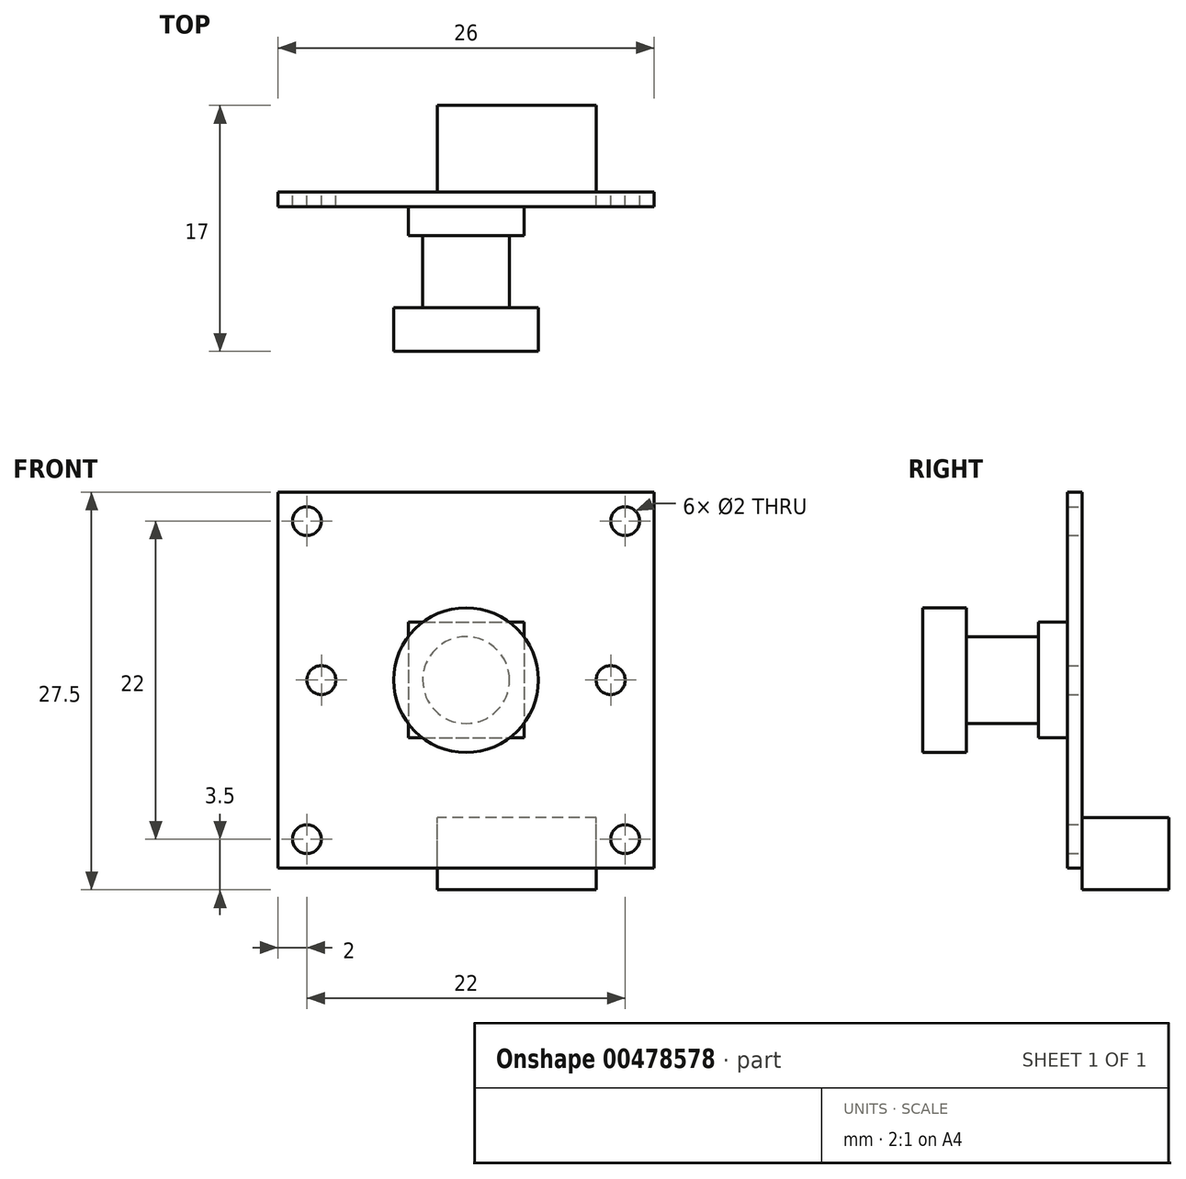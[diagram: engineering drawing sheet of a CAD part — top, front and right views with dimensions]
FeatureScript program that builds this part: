
annotation { "Feature Type Name" : "Feature", "Feature Type Description" : "" }
export const myFeature = defineFeature(function(context is Context, id is Id, definition is map)
    precondition{}
    {
        {
            var Q0;
            Q0=qCreatedBy(makeId("Front.planeOp"),FACE);
            var sketch = newSketch(context, id + "F0", { "sketchPlane" : qUnion([Q0])});
            skLineSegment(sketch, "E0.bottom", {"start": v(-13, 13) * mm, "end": v(13, 13) * mm});
            skLineSegment(sketch, "E0.top", {"start": v(-13, -13) * mm, "end": v(13, -13) * mm});
            skLineSegment(sketch, "E0.left", {"start": v(-13, 13) * mm, "end": v(-13, -13) * mm});
            skLineSegment(sketch, "E0.right", {"start": v(13, 13) * mm, "end": v(13, -13) * mm});
            skPoint(sketch, "E0.middle", {"position": v(0, 0) * mm});
            skLineSegment(sketch, "E1.bottom", {"start": v(-11, 11) * mm, "end": v(11, 11) * mm, "construction": true});
            skLineSegment(sketch, "E1.top", {"start": v(-11, -11) * mm, "end": v(11, -11) * mm, "construction": true});
            skLineSegment(sketch, "E1.left", {"start": v(-11, 11) * mm, "end": v(-11, -11) * mm, "construction": true});
            skLineSegment(sketch, "E1.right", {"start": v(11, 11) * mm, "end": v(11, -11) * mm, "construction": true});
            skCircle(sketch, "E2", {"center": v(-11, 11) * mm, "radius": 1 * mm});
            skCircle(sketch, "E3", {"center": v(11, 11) * mm, "radius": 1 * mm});
            skCircle(sketch, "E4", {"center": v(11, -11) * mm, "radius": 1 * mm});
            skCircle(sketch, "E5", {"center": v(-11, -11) * mm, "radius": 1 * mm});
            skLineSegment(sketch, "E6", {"start": v(0, 0) * mm, "end": v(-10, 0) * mm, "construction": true});
            skCircle(sketch, "E7", {"center": v(-10, 0) * mm, "radius": 1 * mm});
            skLineSegment(sketch, "E8", {"start": v(0, 0) * mm, "end": v(10, 0) * mm, "construction": true});
            skCircle(sketch, "E9", {"center": v(10, 0) * mm, "radius": 1 * mm});
            skSolve(sketch);
        }
        {
            var Q0;
            Q0 = qSketchRegion(id + "F0", true);
            extrude(context, id + "F1", {"entities" : qUnion([Q0]), "depth" : 1 * mm, "offsetDistance" : 25 * mm});
        }
        {
            var Q0;
            Q0=makeQuery(id+"F1.opExtrude","CAP_FACE",FACE,{"disambiguationData":[OSD([sQuery(id+"F0.wireOp",EDGE,"E0.bottom"),sQuery(id+"F0.wireOp",EDGE,"E0.top"),sQuery(id+"F0.wireOp",EDGE,"E0.left"),sQuery(id+"F0.wireOp",EDGE,"E0.right"),sQuery(id+"F0.wireOp",EDGE,"E2"),sQuery(id+"F0.wireOp",EDGE,"E3"),sQuery(id+"F0.wireOp",EDGE,"E4"),sQuery(id+"F0.wireOp",EDGE,"E5")])],"isStart":true});
            var sketch = newSketch(context, id + "F2", { "sketchPlane" : qUnion([Q0])});
            skLineSegment(sketch, "E10.bottom", {"start": v(-9, -14.5) * mm, "end": v(2, -14.5) * mm});
            skLineSegment(sketch, "E10.top", {"start": v(-9, -9.5) * mm, "end": v(2, -9.5) * mm});
            skLineSegment(sketch, "E10.left", {"start": v(-9, -14.5) * mm, "end": v(-9, -9.5) * mm});
            skLineSegment(sketch, "E10.right", {"start": v(2, -14.5) * mm, "end": v(2, -9.5) * mm});
            skPoint(sketch, "E10.middle", {"position": v(-3.5, -12) * mm});
            skSolve(sketch);
        }
        {
            var Q0;
            Q0 = qSketchRegion(id + "F2", true);
            extrude(context, id + "F3", {"entities" : qUnion([Q0]), "operationType" : NewBodyOperationType.ADD, "depth" : 6 * mm, "offsetDistance" : 25 * mm});
        }
        {
            var Q0;
            Q0=makeQuery(id+"F1.opExtrude","CAP_FACE",FACE,{"disambiguationData":[OSD([sQuery(id+"F0.wireOp",EDGE,"E0.bottom"),sQuery(id+"F0.wireOp",EDGE,"E0.top"),sQuery(id+"F0.wireOp",EDGE,"E0.left"),sQuery(id+"F0.wireOp",EDGE,"E0.right"),sQuery(id+"F0.wireOp",EDGE,"E2"),sQuery(id+"F0.wireOp",EDGE,"E3"),sQuery(id+"F0.wireOp",EDGE,"E4"),sQuery(id+"F0.wireOp",EDGE,"E5"),sQuery(id+"F0.wireOp",EDGE,"E7"),sQuery(id+"F0.wireOp",EDGE,"E9")])],"isStart":false});
            var sketch = newSketch(context, id + "F4", { "sketchPlane" : qUnion([Q0])});
            skLineSegment(sketch, "E11.bottom", {"start": v(-4, 4) * mm, "end": v(4, 4) * mm});
            skLineSegment(sketch, "E11.top", {"start": v(-4, -4) * mm, "end": v(4, -4) * mm});
            skLineSegment(sketch, "E11.left", {"start": v(-4, 4) * mm, "end": v(-4, -4) * mm});
            skLineSegment(sketch, "E11.right", {"start": v(4, 4) * mm, "end": v(4, -4) * mm});
            skPoint(sketch, "E11.middle", {"position": v(0, 0) * mm});
            skSolve(sketch);
        }
        {
            var Q0;
            Q0 = qSketchRegion(id + "F4", true);
            extrude(context, id + "F5", {"entities" : qUnion([Q0]), "operationType" : NewBodyOperationType.ADD, "depth" : 2 * mm, "offsetDistance" : 25 * mm});
        }
        {
            var Q0;
            Q0=makeQuery(id+"F5.opExtrude","CAP_FACE",FACE,{"disambiguationData":[OSD([sQuery(id+"F4.wireOp",EDGE,"E11.bottom"),sQuery(id+"F4.wireOp",EDGE,"E11.top"),sQuery(id+"F4.wireOp",EDGE,"E11.left"),sQuery(id+"F4.wireOp",EDGE,"E11.right")])],"isStart":false});
            var sketch = newSketch(context, id + "F6", { "sketchPlane" : qUnion([Q0])});
            skCircle(sketch, "E12", {"center": v(0, 0) * mm, "radius": 3 * mm});
            skSolve(sketch);
        }
        {
            var Q0;
            Q0=makeQuery(id+"F6.imprint","IMPRINT",FACE,{"disambiguationData":[TD([[makeQuery(id+"F6.imprint","IMPRINT",EDGE,{"derivedFrom":sQuery(id+"F6.wireOp",EDGE,"E12")}),1.0]])]});
            extrude(context, id + "F7", {"entities" : qUnion([Q0]), "operationType" : NewBodyOperationType.ADD, "depth" : 5 * mm, "offsetDistance" : 25 * mm});
        }
        {
            var Q0;
            Q0=makeQuery(id+"F7.opExtrude","CAP_FACE",FACE,{"disambiguationData":[OSD([sQuery(id+"F6.wireOp",EDGE,"E12")])],"isStart":false});
            var sketch = newSketch(context, id + "F8", { "sketchPlane" : qUnion([Q0])});
            skCircle(sketch, "E13", {"center": v(0, 0) * mm, "radius": 5 * mm});
            skSolve(sketch);
        }
        {
            var Q0;
            Q0 = qSketchRegion(id + "F8", true);
            extrude(context, id + "F9", {"entities" : qUnion([Q0]), "operationType" : NewBodyOperationType.ADD, "depth" : 3 * mm, "offsetDistance" : 25 * mm});
        }
    });
